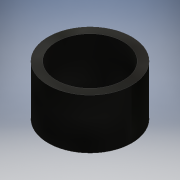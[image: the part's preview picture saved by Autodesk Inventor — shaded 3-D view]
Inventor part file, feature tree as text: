
AUTODESK INVENTOR PART (.ipt)
format: ipt  version: 2016 (Build 200138000, 138)  size: 98,816 bytes
history: native  units: mm
features: other x1, extrude x1, sketch x1
ambient origin geometry x8: Origin, YZ Plane, XZ Plane, XY Plane, X Axis, Y Axis, Z Axis, Center Point
bodies: Body1 (feature_tree)
feature tree (3):
  other  "ソリッド1"
  extrude  "押し出し1"  Depth=8.0mm
  sketch  "スケッチ1"
